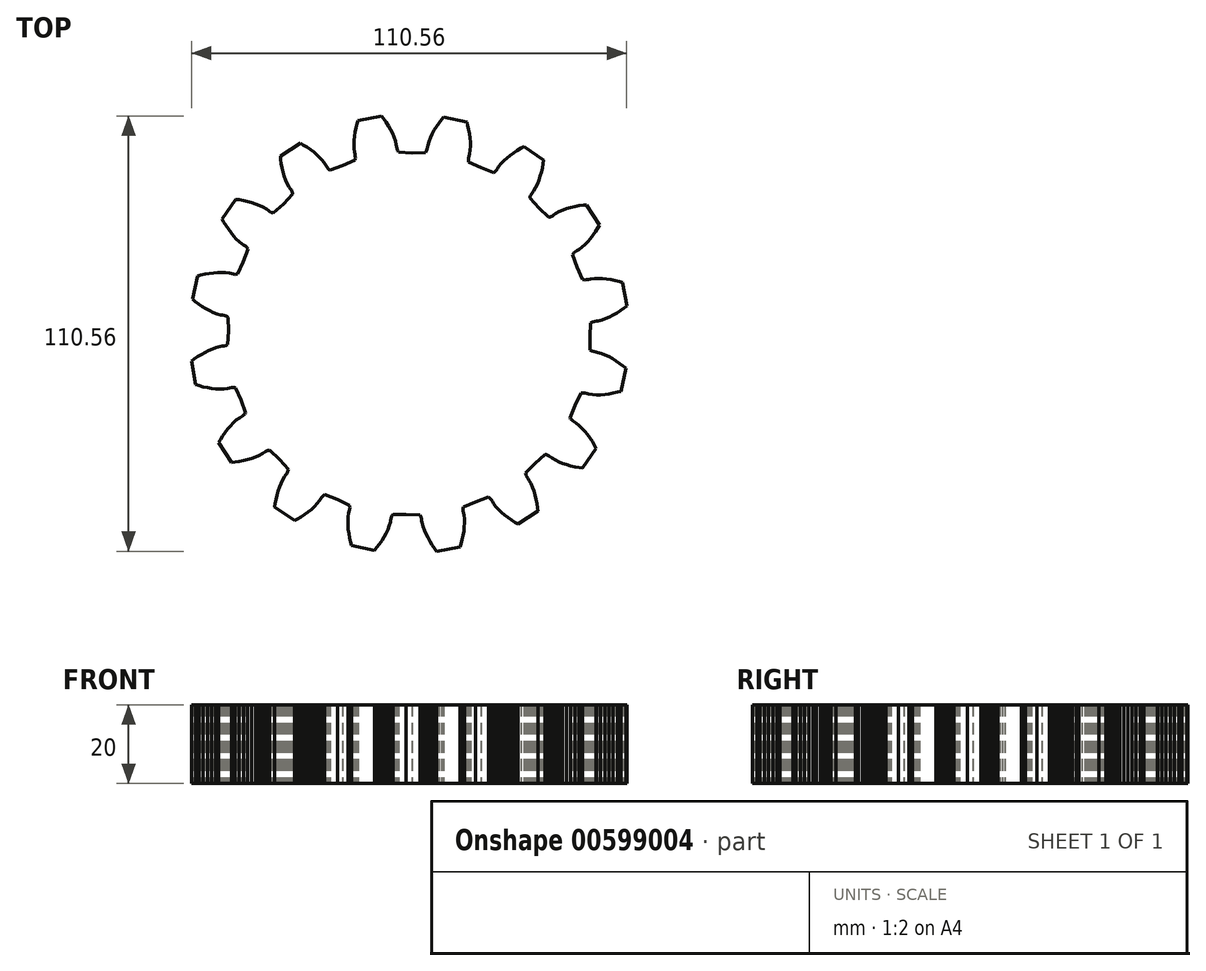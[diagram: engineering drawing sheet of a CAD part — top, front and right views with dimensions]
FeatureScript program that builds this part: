
annotation { "Feature Type Name" : "Feature", "Feature Type Description" : "" }
export const myFeature = defineFeature(function(context is Context, id is Id, definition is map)
    precondition{}
    {
        {
            var Q0;
            Q0=qCreatedBy(makeId("Top.planeOp"),FACE);
            var sketch = newSketch(context, id + "F0", { "sketchPlane" : qUnion([Q0])});
            skLineSegment(sketch, "E0", {"start": v(45.92, -0.72) * mm, "end": v(45.99, -4.15) * mm});
            skLineSegment(sketch, "E1", {"start": v(45.99, -4.15) * mm, "end": v(46.22, -4.32) * mm});
            skLineSegment(sketch, "E2", {"start": v(46.22, -4.32) * mm, "end": v(46.45, -4.43) * mm});
            skLineSegment(sketch, "E3", {"start": v(46.45, -4.43) * mm, "end": v(46.93, -4.6) * mm});
            skLineSegment(sketch, "E4", {"start": v(46.93, -4.6) * mm, "end": v(47.41, -4.7) * mm});
            skLineSegment(sketch, "E5", {"start": v(47.41, -4.7) * mm, "end": v(47.9, -4.78) * mm});
            skLineSegment(sketch, "E6", {"start": v(47.9, -4.78) * mm, "end": v(48.85, -5.05) * mm});
            skLineSegment(sketch, "E7", {"start": v(48.85, -5.05) * mm, "end": v(49.8, -5.41) * mm});
            skLineSegment(sketch, "E8", {"start": v(49.8, -5.41) * mm, "end": v(50.74, -5.86) * mm});
            skLineSegment(sketch, "E9", {"start": v(50.74, -5.86) * mm, "end": v(51.66, -6.36) * mm});
            skLineSegment(sketch, "E10", {"start": v(51.66, -6.36) * mm, "end": v(52.58, -6.93) * mm});
            skLineSegment(sketch, "E11", {"start": v(52.58, -6.93) * mm, "end": v(53.48, -7.54) * mm});
            skLineSegment(sketch, "E12", {"start": v(53.48, -7.54) * mm, "end": v(54.38, -8.21) * mm});
            skLineSegment(sketch, "E13", {"start": v(54.38, -8.21) * mm, "end": v(55.04, -8.75) * mm});
            skLineSegment(sketch, "E14", {"start": v(55.04, -8.75) * mm, "end": v(53.76, -14.67) * mm});
            skLineSegment(sketch, "E15", {"start": v(53.76, -14.67) * mm, "end": v(52.94, -14.89) * mm});
            skLineSegment(sketch, "E16", {"start": v(52.94, -14.89) * mm, "end": v(51.85, -15.13) * mm});
            skLineSegment(sketch, "E17", {"start": v(51.85, -15.13) * mm, "end": v(50.77, -15.32) * mm});
            skLineSegment(sketch, "E18", {"start": v(50.77, -15.32) * mm, "end": v(49.7, -15.46) * mm});
            skLineSegment(sketch, "E19", {"start": v(49.7, -15.46) * mm, "end": v(48.65, -15.54) * mm});
            skLineSegment(sketch, "E20", {"start": v(48.65, -15.54) * mm, "end": v(47.62, -15.56) * mm});
            skLineSegment(sketch, "E21", {"start": v(47.62, -15.56) * mm, "end": v(46.6, -15.5) * mm});
            skLineSegment(sketch, "E22", {"start": v(46.6, -15.5) * mm, "end": v(45.62, -15.36) * mm});
            skLineSegment(sketch, "E23", {"start": v(45.62, -15.36) * mm, "end": v(45.14, -15.23) * mm});
            skLineSegment(sketch, "E24", {"start": v(45.14, -15.23) * mm, "end": v(44.66, -15.12) * mm});
            skLineSegment(sketch, "E25", {"start": v(44.66, -15.12) * mm, "end": v(44.16, -15.07) * mm});
            skLineSegment(sketch, "E26", {"start": v(44.16, -15.07) * mm, "end": v(43.9, -15.08) * mm});
            skLineSegment(sketch, "E27", {"start": v(43.9, -15.08) * mm, "end": v(43.62, -15.14) * mm});
            skLineSegment(sketch, "E28", {"start": v(43.62, -15.14) * mm, "end": v(42.15, -18.24) * mm});
            skLineSegment(sketch, "E29", {"start": v(42.15, -18.24) * mm, "end": v(40.9, -21.43) * mm});
            skLineSegment(sketch, "E30", {"start": v(40.9, -21.43) * mm, "end": v(41.05, -21.68) * mm});
            skLineSegment(sketch, "E31", {"start": v(41.05, -21.68) * mm, "end": v(41.22, -21.87) * mm});
            skLineSegment(sketch, "E32", {"start": v(41.22, -21.87) * mm, "end": v(41.6, -22.2) * mm});
            skLineSegment(sketch, "E33", {"start": v(41.6, -22.2) * mm, "end": v(42, -22.48) * mm});
            skLineSegment(sketch, "E34", {"start": v(42, -22.48) * mm, "end": v(42.42, -22.74) * mm});
            skLineSegment(sketch, "E35", {"start": v(42.42, -22.74) * mm, "end": v(43.2, -23.36) * mm});
            skLineSegment(sketch, "E36", {"start": v(43.2, -23.36) * mm, "end": v(43.94, -24.06) * mm});
            skLineSegment(sketch, "E37", {"start": v(43.94, -24.06) * mm, "end": v(44.63, -24.83) * mm});
            skLineSegment(sketch, "E38", {"start": v(44.63, -24.83) * mm, "end": v(45.3, -25.65) * mm});
            skLineSegment(sketch, "E39", {"start": v(45.3, -25.65) * mm, "end": v(45.93, -26.52) * mm});
            skLineSegment(sketch, "E40", {"start": v(45.93, -26.52) * mm, "end": v(46.52, -27.44) * mm});
            skLineSegment(sketch, "E41", {"start": v(46.52, -27.44) * mm, "end": v(47.1, -28.4) * mm});
            skLineSegment(sketch, "E42", {"start": v(47.1, -28.4) * mm, "end": v(47.5, -29.14) * mm});
            skLineSegment(sketch, "E43", {"start": v(47.5, -29.14) * mm, "end": v(44.05, -34.13) * mm});
            skLineSegment(sketch, "E44", {"start": v(44.05, -34.13) * mm, "end": v(43.21, -34.01) * mm});
            skLineSegment(sketch, "E45", {"start": v(43.21, -34.01) * mm, "end": v(42.11, -33.82) * mm});
            skLineSegment(sketch, "E46", {"start": v(42.11, -33.82) * mm, "end": v(41.04, -33.59) * mm});
            skLineSegment(sketch, "E47", {"start": v(41.04, -33.59) * mm, "end": v(40, -33.3) * mm});
            skLineSegment(sketch, "E48", {"start": v(40, -33.3) * mm, "end": v(39, -32.98) * mm});
            skLineSegment(sketch, "E49", {"start": v(39, -32.98) * mm, "end": v(38.04, -32.6) * mm});
            skLineSegment(sketch, "E50", {"start": v(38.04, -32.6) * mm, "end": v(37.12, -32.16) * mm});
            skLineSegment(sketch, "E51", {"start": v(37.12, -32.16) * mm, "end": v(36.27, -31.65) * mm});
            skLineSegment(sketch, "E52", {"start": v(36.27, -31.65) * mm, "end": v(35.88, -31.35) * mm});
            skLineSegment(sketch, "E53", {"start": v(35.88, -31.35) * mm, "end": v(35.48, -31.06) * mm});
            skLineSegment(sketch, "E54", {"start": v(35.48, -31.06) * mm, "end": v(35.03, -30.83) * mm});
            skLineSegment(sketch, "E55", {"start": v(35.03, -30.83) * mm, "end": v(34.79, -30.74) * mm});
            skLineSegment(sketch, "E56", {"start": v(34.79, -30.74) * mm, "end": v(34.5, -30.68) * mm});
            skLineSegment(sketch, "E57", {"start": v(34.5, -30.68) * mm, "end": v(31.96, -32.98) * mm});
            skLineSegment(sketch, "E58", {"start": v(31.96, -32.98) * mm, "end": v(29.58, -35.45) * mm});
            skLineSegment(sketch, "E59", {"start": v(29.58, -35.45) * mm, "end": v(29.63, -35.73) * mm});
            skLineSegment(sketch, "E60", {"start": v(29.63, -35.73) * mm, "end": v(29.71, -35.98) * mm});
            skLineSegment(sketch, "E61", {"start": v(29.71, -35.98) * mm, "end": v(29.93, -36.43) * mm});
            skLineSegment(sketch, "E62", {"start": v(29.93, -36.43) * mm, "end": v(30.2, -36.85) * mm});
            skLineSegment(sketch, "E63", {"start": v(30.2, -36.85) * mm, "end": v(30.5, -37.25) * mm});
            skLineSegment(sketch, "E64", {"start": v(30.5, -37.25) * mm, "end": v(30.98, -38.11) * mm});
            skLineSegment(sketch, "E65", {"start": v(30.98, -38.11) * mm, "end": v(31.39, -39.04) * mm});
            skLineSegment(sketch, "E66", {"start": v(31.39, -39.04) * mm, "end": v(31.73, -40.02) * mm});
            skLineSegment(sketch, "E67", {"start": v(31.73, -40.02) * mm, "end": v(32.03, -41.03) * mm});
            skLineSegment(sketch, "E68", {"start": v(32.03, -41.03) * mm, "end": v(32.28, -42.08) * mm});
            skLineSegment(sketch, "E69", {"start": v(32.28, -42.08) * mm, "end": v(32.48, -43.15) * mm});
            skLineSegment(sketch, "E70", {"start": v(32.48, -43.15) * mm, "end": v(32.64, -44.26) * mm});
            skLineSegment(sketch, "E71", {"start": v(32.64, -44.26) * mm, "end": v(32.73, -45.1) * mm});
            skLineSegment(sketch, "E72", {"start": v(32.73, -45.1) * mm, "end": v(27.64, -48.4) * mm});
            skLineSegment(sketch, "E73", {"start": v(27.64, -48.4) * mm, "end": v(26.9, -47.96) * mm});
            skLineSegment(sketch, "E74", {"start": v(26.9, -47.96) * mm, "end": v(25.96, -47.36) * mm});
            skLineSegment(sketch, "E75", {"start": v(25.96, -47.36) * mm, "end": v(25.06, -46.74) * mm});
            skLineSegment(sketch, "E76", {"start": v(25.06, -46.74) * mm, "end": v(24.21, -46.08) * mm});
            skLineSegment(sketch, "E77", {"start": v(24.21, -46.08) * mm, "end": v(23.41, -45.4) * mm});
            skLineSegment(sketch, "E78", {"start": v(23.41, -45.4) * mm, "end": v(22.67, -44.67) * mm});
            skLineSegment(sketch, "E79", {"start": v(22.67, -44.67) * mm, "end": v(21.99, -43.92) * mm});
            skLineSegment(sketch, "E80", {"start": v(21.99, -43.92) * mm, "end": v(21.4, -43.12) * mm});
            skLineSegment(sketch, "E81", {"start": v(21.4, -43.12) * mm, "end": v(21.15, -42.7) * mm});
            skLineSegment(sketch, "E82", {"start": v(21.15, -42.7) * mm, "end": v(20.89, -42.28) * mm});
            skLineSegment(sketch, "E83", {"start": v(20.89, -42.28) * mm, "end": v(20.57, -41.89) * mm});
            skLineSegment(sketch, "E84", {"start": v(20.57, -41.89) * mm, "end": v(20.38, -41.7) * mm});
            skLineSegment(sketch, "E85", {"start": v(20.38, -41.7) * mm, "end": v(20.14, -41.55) * mm});
            skLineSegment(sketch, "E86", {"start": v(20.14, -41.55) * mm, "end": v(16.9, -42.7) * mm});
            skLineSegment(sketch, "E87", {"start": v(16.9, -42.7) * mm, "end": v(13.76, -44.08) * mm});
            skLineSegment(sketch, "E88", {"start": v(13.76, -44.08) * mm, "end": v(13.7, -44.35) * mm});
            skLineSegment(sketch, "E89", {"start": v(13.7, -44.35) * mm, "end": v(13.68, -44.61) * mm});
            skLineSegment(sketch, "E90", {"start": v(13.68, -44.61) * mm, "end": v(13.71, -45.12) * mm});
            skLineSegment(sketch, "E91", {"start": v(13.71, -45.12) * mm, "end": v(13.8, -45.6) * mm});
            skLineSegment(sketch, "E92", {"start": v(13.8, -45.6) * mm, "end": v(13.92, -46.08) * mm});
            skLineSegment(sketch, "E93", {"start": v(13.92, -46.08) * mm, "end": v(14.03, -47.07) * mm});
            skLineSegment(sketch, "E94", {"start": v(14.03, -47.07) * mm, "end": v(14.06, -48.08) * mm});
            skLineSegment(sketch, "E95", {"start": v(14.06, -48.08) * mm, "end": v(14, -49.12) * mm});
            skLineSegment(sketch, "E96", {"start": v(14, -49.12) * mm, "end": v(13.9, -50.17) * mm});
            skLineSegment(sketch, "E97", {"start": v(13.9, -50.17) * mm, "end": v(13.72, -51.23) * mm});
            skLineSegment(sketch, "E98", {"start": v(13.72, -51.23) * mm, "end": v(13.5, -52.3) * mm});
            skLineSegment(sketch, "E99", {"start": v(13.5, -52.3) * mm, "end": v(13.22, -53.38) * mm});
            skLineSegment(sketch, "E100", {"start": v(13.22, -53.38) * mm, "end": v(12.98, -54.2) * mm});
            skLineSegment(sketch, "E101", {"start": v(12.98, -54.2) * mm, "end": v(7.02, -55.28) * mm});
            skLineSegment(sketch, "E102", {"start": v(7.02, -55.28) * mm, "end": v(6.5, -54.6) * mm});
            skLineSegment(sketch, "E103", {"start": v(6.5, -54.6) * mm, "end": v(5.86, -53.7) * mm});
            skLineSegment(sketch, "E104", {"start": v(5.86, -53.7) * mm, "end": v(5.27, -52.77) * mm});
            skLineSegment(sketch, "E105", {"start": v(5.27, -52.77) * mm, "end": v(4.74, -51.84) * mm});
            skLineSegment(sketch, "E106", {"start": v(4.74, -51.84) * mm, "end": v(4.26, -50.9) * mm});
            skLineSegment(sketch, "E107", {"start": v(4.26, -50.9) * mm, "end": v(3.85, -49.95) * mm});
            skLineSegment(sketch, "E108", {"start": v(3.85, -49.95) * mm, "end": v(3.5, -48.99) * mm});
            skLineSegment(sketch, "E109", {"start": v(3.5, -48.99) * mm, "end": v(3.27, -48.02) * mm});
            skLineSegment(sketch, "E110", {"start": v(3.27, -48.02) * mm, "end": v(3.2, -47.54) * mm});
            skLineSegment(sketch, "E111", {"start": v(3.2, -47.54) * mm, "end": v(3.12, -47.05) * mm});
            skLineSegment(sketch, "E112", {"start": v(3.12, -47.05) * mm, "end": v(2.97, -46.57) * mm});
            skLineSegment(sketch, "E113", {"start": v(2.97, -46.57) * mm, "end": v(2.86, -46.33) * mm});
            skLineSegment(sketch, "E114", {"start": v(2.86, -46.33) * mm, "end": v(2.7, -46.1) * mm});
            skLineSegment(sketch, "E115", {"start": v(2.7, -46.1) * mm, "end": v(-0.72, -45.92) * mm});
            skLineSegment(sketch, "E116", {"start": v(-0.72, -45.92) * mm, "end": v(-4.15, -45.99) * mm});
            skLineSegment(sketch, "E117", {"start": v(-4.15, -45.99) * mm, "end": v(-4.32, -46.22) * mm});
            skLineSegment(sketch, "E118", {"start": v(-4.32, -46.22) * mm, "end": v(-4.43, -46.45) * mm});
            skLineSegment(sketch, "E119", {"start": v(-4.43, -46.45) * mm, "end": v(-4.6, -46.93) * mm});
            skLineSegment(sketch, "E120", {"start": v(-4.6, -46.93) * mm, "end": v(-4.7, -47.41) * mm});
            skLineSegment(sketch, "E121", {"start": v(-4.7, -47.41) * mm, "end": v(-4.78, -47.9) * mm});
            skLineSegment(sketch, "E122", {"start": v(-4.78, -47.9) * mm, "end": v(-5.05, -48.85) * mm});
            skLineSegment(sketch, "E123", {"start": v(-5.05, -48.85) * mm, "end": v(-5.41, -49.8) * mm});
            skLineSegment(sketch, "E124", {"start": v(-5.41, -49.8) * mm, "end": v(-5.86, -50.74) * mm});
            skLineSegment(sketch, "E125", {"start": v(-5.86, -50.74) * mm, "end": v(-6.36, -51.66) * mm});
            skLineSegment(sketch, "E126", {"start": v(-6.36, -51.66) * mm, "end": v(-6.93, -52.58) * mm});
            skLineSegment(sketch, "E127", {"start": v(-6.93, -52.58) * mm, "end": v(-7.54, -53.48) * mm});
            skLineSegment(sketch, "E128", {"start": v(-7.54, -53.48) * mm, "end": v(-8.21, -54.38) * mm});
            skLineSegment(sketch, "E129", {"start": v(-8.21, -54.38) * mm, "end": v(-8.75, -55.04) * mm});
            skLineSegment(sketch, "E130", {"start": v(-8.75, -55.04) * mm, "end": v(-14.67, -53.76) * mm});
            skLineSegment(sketch, "E131", {"start": v(-14.67, -53.76) * mm, "end": v(-14.89, -52.94) * mm});
            skLineSegment(sketch, "E132", {"start": v(-14.89, -52.94) * mm, "end": v(-15.13, -51.85) * mm});
            skLineSegment(sketch, "E133", {"start": v(-15.13, -51.85) * mm, "end": v(-15.32, -50.77) * mm});
            skLineSegment(sketch, "E134", {"start": v(-15.32, -50.77) * mm, "end": v(-15.46, -49.7) * mm});
            skLineSegment(sketch, "E135", {"start": v(-15.46, -49.7) * mm, "end": v(-15.54, -48.65) * mm});
            skLineSegment(sketch, "E136", {"start": v(-15.54, -48.65) * mm, "end": v(-15.56, -47.62) * mm});
            skLineSegment(sketch, "E137", {"start": v(-15.56, -47.62) * mm, "end": v(-15.5, -46.6) * mm});
            skLineSegment(sketch, "E138", {"start": v(-15.5, -46.6) * mm, "end": v(-15.36, -45.62) * mm});
            skLineSegment(sketch, "E139", {"start": v(-15.36, -45.62) * mm, "end": v(-15.23, -45.14) * mm});
            skLineSegment(sketch, "E140", {"start": v(-15.23, -45.14) * mm, "end": v(-15.12, -44.66) * mm});
            skLineSegment(sketch, "E141", {"start": v(-15.12, -44.66) * mm, "end": v(-15.07, -44.16) * mm});
            skLineSegment(sketch, "E142", {"start": v(-15.07, -44.16) * mm, "end": v(-15.08, -43.9) * mm});
            skLineSegment(sketch, "E143", {"start": v(-15.08, -43.9) * mm, "end": v(-15.14, -43.62) * mm});
            skLineSegment(sketch, "E144", {"start": v(-15.14, -43.62) * mm, "end": v(-18.24, -42.15) * mm});
            skLineSegment(sketch, "E145", {"start": v(-18.24, -42.15) * mm, "end": v(-21.43, -40.9) * mm});
            skLineSegment(sketch, "E146", {"start": v(-21.43, -40.9) * mm, "end": v(-21.68, -41.05) * mm});
            skLineSegment(sketch, "E147", {"start": v(-21.68, -41.05) * mm, "end": v(-21.87, -41.22) * mm});
            skLineSegment(sketch, "E148", {"start": v(-21.87, -41.22) * mm, "end": v(-22.2, -41.6) * mm});
            skLineSegment(sketch, "E149", {"start": v(-22.2, -41.6) * mm, "end": v(-22.48, -42) * mm});
            skLineSegment(sketch, "E150", {"start": v(-22.48, -42) * mm, "end": v(-22.74, -42.42) * mm});
            skLineSegment(sketch, "E151", {"start": v(-22.74, -42.42) * mm, "end": v(-23.36, -43.2) * mm});
            skLineSegment(sketch, "E152", {"start": v(-23.36, -43.2) * mm, "end": v(-24.06, -43.94) * mm});
            skLineSegment(sketch, "E153", {"start": v(-24.06, -43.94) * mm, "end": v(-24.83, -44.63) * mm});
            skLineSegment(sketch, "E154", {"start": v(-24.83, -44.63) * mm, "end": v(-25.65, -45.3) * mm});
            skLineSegment(sketch, "E155", {"start": v(-25.65, -45.3) * mm, "end": v(-26.52, -45.93) * mm});
            skLineSegment(sketch, "E156", {"start": v(-26.52, -45.93) * mm, "end": v(-27.44, -46.52) * mm});
            skLineSegment(sketch, "E157", {"start": v(-27.44, -46.52) * mm, "end": v(-28.4, -47.1) * mm});
            skLineSegment(sketch, "E158", {"start": v(-28.4, -47.1) * mm, "end": v(-29.14, -47.5) * mm});
            skLineSegment(sketch, "E159", {"start": v(-29.14, -47.5) * mm, "end": v(-34.13, -44.05) * mm});
            skLineSegment(sketch, "E160", {"start": v(-34.13, -44.05) * mm, "end": v(-34.01, -43.21) * mm});
            skLineSegment(sketch, "E161", {"start": v(-34.01, -43.21) * mm, "end": v(-33.82, -42.11) * mm});
            skLineSegment(sketch, "E162", {"start": v(-33.82, -42.11) * mm, "end": v(-33.59, -41.04) * mm});
            skLineSegment(sketch, "E163", {"start": v(-33.59, -41.04) * mm, "end": v(-33.3, -40) * mm});
            skLineSegment(sketch, "E164", {"start": v(-33.3, -40) * mm, "end": v(-32.98, -39) * mm});
            skLineSegment(sketch, "E165", {"start": v(-32.98, -39) * mm, "end": v(-32.6, -38.04) * mm});
            skLineSegment(sketch, "E166", {"start": v(-32.6, -38.04) * mm, "end": v(-32.16, -37.12) * mm});
            skLineSegment(sketch, "E167", {"start": v(-32.16, -37.12) * mm, "end": v(-31.65, -36.27) * mm});
            skLineSegment(sketch, "E168", {"start": v(-31.65, -36.27) * mm, "end": v(-31.35, -35.88) * mm});
            skLineSegment(sketch, "E169", {"start": v(-31.35, -35.88) * mm, "end": v(-31.06, -35.48) * mm});
            skLineSegment(sketch, "E170", {"start": v(-31.06, -35.48) * mm, "end": v(-30.83, -35.03) * mm});
            skLineSegment(sketch, "E171", {"start": v(-30.83, -35.03) * mm, "end": v(-30.74, -34.79) * mm});
            skLineSegment(sketch, "E172", {"start": v(-30.74, -34.79) * mm, "end": v(-30.68, -34.5) * mm});
            skLineSegment(sketch, "E173", {"start": v(-30.68, -34.5) * mm, "end": v(-32.98, -31.96) * mm});
            skLineSegment(sketch, "E174", {"start": v(-32.98, -31.96) * mm, "end": v(-35.45, -29.58) * mm});
            skLineSegment(sketch, "E175", {"start": v(-35.45, -29.58) * mm, "end": v(-35.73, -29.63) * mm});
            skLineSegment(sketch, "E176", {"start": v(-35.73, -29.63) * mm, "end": v(-35.98, -29.71) * mm});
            skLineSegment(sketch, "E177", {"start": v(-35.98, -29.71) * mm, "end": v(-36.43, -29.93) * mm});
            skLineSegment(sketch, "E178", {"start": v(-36.43, -29.93) * mm, "end": v(-36.85, -30.2) * mm});
            skLineSegment(sketch, "E179", {"start": v(-36.85, -30.2) * mm, "end": v(-37.25, -30.5) * mm});
            skLineSegment(sketch, "E180", {"start": v(-37.25, -30.5) * mm, "end": v(-38.11, -30.98) * mm});
            skLineSegment(sketch, "E181", {"start": v(-38.11, -30.98) * mm, "end": v(-39.04, -31.39) * mm});
            skLineSegment(sketch, "E182", {"start": v(-39.04, -31.39) * mm, "end": v(-40.02, -31.73) * mm});
            skLineSegment(sketch, "E183", {"start": v(-40.02, -31.73) * mm, "end": v(-41.03, -32.03) * mm});
            skLineSegment(sketch, "E184", {"start": v(-41.03, -32.03) * mm, "end": v(-42.08, -32.28) * mm});
            skLineSegment(sketch, "E185", {"start": v(-42.08, -32.28) * mm, "end": v(-43.15, -32.48) * mm});
            skLineSegment(sketch, "E186", {"start": v(-43.15, -32.48) * mm, "end": v(-44.26, -32.64) * mm});
            skLineSegment(sketch, "E187", {"start": v(-44.26, -32.64) * mm, "end": v(-45.1, -32.73) * mm});
            skLineSegment(sketch, "E188", {"start": v(-45.1, -32.73) * mm, "end": v(-48.4, -27.64) * mm});
            skLineSegment(sketch, "E189", {"start": v(-48.4, -27.64) * mm, "end": v(-47.96, -26.9) * mm});
            skLineSegment(sketch, "E190", {"start": v(-47.96, -26.9) * mm, "end": v(-47.36, -25.96) * mm});
            skLineSegment(sketch, "E191", {"start": v(-47.36, -25.96) * mm, "end": v(-46.74, -25.06) * mm});
            skLineSegment(sketch, "E192", {"start": v(-46.74, -25.06) * mm, "end": v(-46.08, -24.21) * mm});
            skLineSegment(sketch, "E193", {"start": v(-46.08, -24.21) * mm, "end": v(-45.4, -23.41) * mm});
            skLineSegment(sketch, "E194", {"start": v(-45.4, -23.41) * mm, "end": v(-44.67, -22.67) * mm});
            skLineSegment(sketch, "E195", {"start": v(-44.67, -22.67) * mm, "end": v(-43.92, -21.99) * mm});
            skLineSegment(sketch, "E196", {"start": v(-43.92, -21.99) * mm, "end": v(-43.12, -21.4) * mm});
            skLineSegment(sketch, "E197", {"start": v(-43.12, -21.4) * mm, "end": v(-42.7, -21.15) * mm});
            skLineSegment(sketch, "E198", {"start": v(-42.7, -21.15) * mm, "end": v(-42.28, -20.89) * mm});
            skLineSegment(sketch, "E199", {"start": v(-42.28, -20.89) * mm, "end": v(-41.89, -20.57) * mm});
            skLineSegment(sketch, "E200", {"start": v(-41.89, -20.57) * mm, "end": v(-41.7, -20.38) * mm});
            skLineSegment(sketch, "E201", {"start": v(-41.7, -20.38) * mm, "end": v(-41.55, -20.14) * mm});
            skLineSegment(sketch, "E202", {"start": v(-41.55, -20.14) * mm, "end": v(-42.7, -16.9) * mm});
            skLineSegment(sketch, "E203", {"start": v(-42.7, -16.9) * mm, "end": v(-44.08, -13.76) * mm});
            skLineSegment(sketch, "E204", {"start": v(-44.08, -13.76) * mm, "end": v(-44.35, -13.7) * mm});
            skLineSegment(sketch, "E205", {"start": v(-44.35, -13.7) * mm, "end": v(-44.61, -13.68) * mm});
            skLineSegment(sketch, "E206", {"start": v(-44.61, -13.68) * mm, "end": v(-45.12, -13.71) * mm});
            skLineSegment(sketch, "E207", {"start": v(-45.12, -13.71) * mm, "end": v(-45.6, -13.8) * mm});
            skLineSegment(sketch, "E208", {"start": v(-45.6, -13.8) * mm, "end": v(-46.08, -13.92) * mm});
            skLineSegment(sketch, "E209", {"start": v(-46.08, -13.92) * mm, "end": v(-47.07, -14.03) * mm});
            skLineSegment(sketch, "E210", {"start": v(-47.07, -14.03) * mm, "end": v(-48.08, -14.06) * mm});
            skLineSegment(sketch, "E211", {"start": v(-48.08, -14.06) * mm, "end": v(-49.12, -14) * mm});
            skLineSegment(sketch, "E212", {"start": v(-49.12, -14) * mm, "end": v(-50.17, -13.9) * mm});
            skLineSegment(sketch, "E213", {"start": v(-50.17, -13.9) * mm, "end": v(-51.23, -13.72) * mm});
            skLineSegment(sketch, "E214", {"start": v(-51.23, -13.72) * mm, "end": v(-52.3, -13.5) * mm});
            skLineSegment(sketch, "E215", {"start": v(-52.3, -13.5) * mm, "end": v(-53.38, -13.22) * mm});
            skLineSegment(sketch, "E216", {"start": v(-53.38, -13.22) * mm, "end": v(-54.2, -12.98) * mm});
            skLineSegment(sketch, "E217", {"start": v(-54.2, -12.98) * mm, "end": v(-55.28, -7.02) * mm});
            skLineSegment(sketch, "E218", {"start": v(-55.28, -7.02) * mm, "end": v(-54.6, -6.5) * mm});
            skLineSegment(sketch, "E219", {"start": v(-54.6, -6.5) * mm, "end": v(-53.7, -5.86) * mm});
            skLineSegment(sketch, "E220", {"start": v(-53.7, -5.86) * mm, "end": v(-52.77, -5.27) * mm});
            skLineSegment(sketch, "E221", {"start": v(-52.77, -5.27) * mm, "end": v(-51.84, -4.74) * mm});
            skLineSegment(sketch, "E222", {"start": v(-51.84, -4.74) * mm, "end": v(-50.9, -4.26) * mm});
            skLineSegment(sketch, "E223", {"start": v(-50.9, -4.26) * mm, "end": v(-49.95, -3.85) * mm});
            skLineSegment(sketch, "E224", {"start": v(-49.95, -3.85) * mm, "end": v(-48.99, -3.5) * mm});
            skLineSegment(sketch, "E225", {"start": v(-48.99, -3.5) * mm, "end": v(-48.02, -3.27) * mm});
            skLineSegment(sketch, "E226", {"start": v(-48.02, -3.27) * mm, "end": v(-47.54, -3.2) * mm});
            skLineSegment(sketch, "E227", {"start": v(-47.54, -3.2) * mm, "end": v(-47.05, -3.12) * mm});
            skLineSegment(sketch, "E228", {"start": v(-47.05, -3.12) * mm, "end": v(-46.57, -2.97) * mm});
            skLineSegment(sketch, "E229", {"start": v(-46.57, -2.97) * mm, "end": v(-46.33, -2.86) * mm});
            skLineSegment(sketch, "E230", {"start": v(-46.33, -2.86) * mm, "end": v(-46.1, -2.7) * mm});
            skLineSegment(sketch, "E231", {"start": v(-46.1, -2.7) * mm, "end": v(-45.92, 0.72) * mm});
            skLineSegment(sketch, "E232", {"start": v(-45.92, 0.72) * mm, "end": v(-45.99, 4.15) * mm});
            skLineSegment(sketch, "E233", {"start": v(-45.99, 4.15) * mm, "end": v(-46.22, 4.32) * mm});
            skLineSegment(sketch, "E234", {"start": v(-46.22, 4.32) * mm, "end": v(-46.45, 4.43) * mm});
            skLineSegment(sketch, "E235", {"start": v(-46.45, 4.43) * mm, "end": v(-46.93, 4.6) * mm});
            skLineSegment(sketch, "E236", {"start": v(-46.93, 4.6) * mm, "end": v(-47.41, 4.7) * mm});
            skLineSegment(sketch, "E237", {"start": v(-47.41, 4.7) * mm, "end": v(-47.9, 4.78) * mm});
            skLineSegment(sketch, "E238", {"start": v(-47.9, 4.78) * mm, "end": v(-48.85, 5.05) * mm});
            skLineSegment(sketch, "E239", {"start": v(-48.85, 5.05) * mm, "end": v(-49.8, 5.41) * mm});
            skLineSegment(sketch, "E240", {"start": v(-49.8, 5.41) * mm, "end": v(-50.74, 5.86) * mm});
            skLineSegment(sketch, "E241", {"start": v(-50.74, 5.86) * mm, "end": v(-51.66, 6.36) * mm});
            skLineSegment(sketch, "E242", {"start": v(-51.66, 6.36) * mm, "end": v(-52.58, 6.93) * mm});
            skLineSegment(sketch, "E243", {"start": v(-52.58, 6.93) * mm, "end": v(-53.48, 7.54) * mm});
            skLineSegment(sketch, "E244", {"start": v(-53.48, 7.54) * mm, "end": v(-54.38, 8.21) * mm});
            skLineSegment(sketch, "E245", {"start": v(-54.38, 8.21) * mm, "end": v(-55.04, 8.75) * mm});
            skLineSegment(sketch, "E246", {"start": v(-55.04, 8.75) * mm, "end": v(-53.76, 14.67) * mm});
            skLineSegment(sketch, "E247", {"start": v(-53.76, 14.67) * mm, "end": v(-52.94, 14.89) * mm});
            skLineSegment(sketch, "E248", {"start": v(-52.94, 14.89) * mm, "end": v(-51.85, 15.13) * mm});
            skLineSegment(sketch, "E249", {"start": v(-51.85, 15.13) * mm, "end": v(-50.77, 15.32) * mm});
            skLineSegment(sketch, "E250", {"start": v(-50.77, 15.32) * mm, "end": v(-49.7, 15.46) * mm});
            skLineSegment(sketch, "E251", {"start": v(-49.7, 15.46) * mm, "end": v(-48.65, 15.54) * mm});
            skLineSegment(sketch, "E252", {"start": v(-48.65, 15.54) * mm, "end": v(-47.62, 15.56) * mm});
            skLineSegment(sketch, "E253", {"start": v(-47.62, 15.56) * mm, "end": v(-46.6, 15.5) * mm});
            skLineSegment(sketch, "E254", {"start": v(-46.6, 15.5) * mm, "end": v(-45.62, 15.36) * mm});
            skLineSegment(sketch, "E255", {"start": v(-45.62, 15.36) * mm, "end": v(-45.14, 15.23) * mm});
            skLineSegment(sketch, "E256", {"start": v(-45.14, 15.23) * mm, "end": v(-44.66, 15.12) * mm});
            skLineSegment(sketch, "E257", {"start": v(-44.66, 15.12) * mm, "end": v(-44.16, 15.07) * mm});
            skLineSegment(sketch, "E258", {"start": v(-44.16, 15.07) * mm, "end": v(-43.9, 15.08) * mm});
            skLineSegment(sketch, "E259", {"start": v(-43.9, 15.08) * mm, "end": v(-43.62, 15.14) * mm});
            skLineSegment(sketch, "E260", {"start": v(-43.62, 15.14) * mm, "end": v(-42.15, 18.24) * mm});
            skLineSegment(sketch, "E261", {"start": v(-42.15, 18.24) * mm, "end": v(-40.9, 21.43) * mm});
            skLineSegment(sketch, "E262", {"start": v(-40.9, 21.43) * mm, "end": v(-41.05, 21.68) * mm});
            skLineSegment(sketch, "E263", {"start": v(-41.05, 21.68) * mm, "end": v(-41.22, 21.87) * mm});
            skLineSegment(sketch, "E264", {"start": v(-41.22, 21.87) * mm, "end": v(-41.6, 22.2) * mm});
            skLineSegment(sketch, "E265", {"start": v(-41.6, 22.2) * mm, "end": v(-42, 22.48) * mm});
            skLineSegment(sketch, "E266", {"start": v(-42, 22.48) * mm, "end": v(-42.42, 22.74) * mm});
            skLineSegment(sketch, "E267", {"start": v(-42.42, 22.74) * mm, "end": v(-43.2, 23.36) * mm});
            skLineSegment(sketch, "E268", {"start": v(-43.2, 23.36) * mm, "end": v(-43.94, 24.06) * mm});
            skLineSegment(sketch, "E269", {"start": v(-43.94, 24.06) * mm, "end": v(-44.63, 24.83) * mm});
            skLineSegment(sketch, "E270", {"start": v(-44.63, 24.83) * mm, "end": v(-45.3, 25.65) * mm});
            skLineSegment(sketch, "E271", {"start": v(-45.3, 25.65) * mm, "end": v(-45.93, 26.52) * mm});
            skLineSegment(sketch, "E272", {"start": v(-45.93, 26.52) * mm, "end": v(-46.52, 27.44) * mm});
            skLineSegment(sketch, "E273", {"start": v(-46.52, 27.44) * mm, "end": v(-47.1, 28.4) * mm});
            skLineSegment(sketch, "E274", {"start": v(-47.1, 28.4) * mm, "end": v(-47.5, 29.14) * mm});
            skLineSegment(sketch, "E275", {"start": v(-47.5, 29.14) * mm, "end": v(-44.05, 34.13) * mm});
            skLineSegment(sketch, "E276", {"start": v(-44.05, 34.13) * mm, "end": v(-43.21, 34.01) * mm});
            skLineSegment(sketch, "E277", {"start": v(-43.21, 34.01) * mm, "end": v(-42.11, 33.82) * mm});
            skLineSegment(sketch, "E278", {"start": v(-42.11, 33.82) * mm, "end": v(-41.04, 33.59) * mm});
            skLineSegment(sketch, "E279", {"start": v(-41.04, 33.59) * mm, "end": v(-40, 33.3) * mm});
            skLineSegment(sketch, "E280", {"start": v(-40, 33.3) * mm, "end": v(-39, 32.98) * mm});
            skLineSegment(sketch, "E281", {"start": v(-39, 32.98) * mm, "end": v(-38.04, 32.6) * mm});
            skLineSegment(sketch, "E282", {"start": v(-38.04, 32.6) * mm, "end": v(-37.12, 32.16) * mm});
            skLineSegment(sketch, "E283", {"start": v(-37.12, 32.16) * mm, "end": v(-36.27, 31.65) * mm});
            skLineSegment(sketch, "E284", {"start": v(-36.27, 31.65) * mm, "end": v(-35.88, 31.35) * mm});
            skLineSegment(sketch, "E285", {"start": v(-35.88, 31.35) * mm, "end": v(-35.48, 31.06) * mm});
            skLineSegment(sketch, "E286", {"start": v(-35.48, 31.06) * mm, "end": v(-35.03, 30.83) * mm});
            skLineSegment(sketch, "E287", {"start": v(-35.03, 30.83) * mm, "end": v(-34.79, 30.74) * mm});
            skLineSegment(sketch, "E288", {"start": v(-34.79, 30.74) * mm, "end": v(-34.5, 30.68) * mm});
            skLineSegment(sketch, "E289", {"start": v(-34.5, 30.68) * mm, "end": v(-31.96, 32.98) * mm});
            skLineSegment(sketch, "E290", {"start": v(-31.96, 32.98) * mm, "end": v(-29.58, 35.45) * mm});
            skLineSegment(sketch, "E291", {"start": v(-29.58, 35.45) * mm, "end": v(-29.63, 35.73) * mm});
            skLineSegment(sketch, "E292", {"start": v(-29.63, 35.73) * mm, "end": v(-29.71, 35.98) * mm});
            skLineSegment(sketch, "E293", {"start": v(-29.71, 35.98) * mm, "end": v(-29.93, 36.43) * mm});
            skLineSegment(sketch, "E294", {"start": v(-29.93, 36.43) * mm, "end": v(-30.2, 36.85) * mm});
            skLineSegment(sketch, "E295", {"start": v(-30.2, 36.85) * mm, "end": v(-30.5, 37.25) * mm});
            skLineSegment(sketch, "E296", {"start": v(-30.5, 37.25) * mm, "end": v(-30.98, 38.11) * mm});
            skLineSegment(sketch, "E297", {"start": v(-30.98, 38.11) * mm, "end": v(-31.39, 39.04) * mm});
            skLineSegment(sketch, "E298", {"start": v(-31.39, 39.04) * mm, "end": v(-31.73, 40.02) * mm});
            skLineSegment(sketch, "E299", {"start": v(-31.73, 40.02) * mm, "end": v(-32.03, 41.03) * mm});
            skLineSegment(sketch, "E300", {"start": v(-32.03, 41.03) * mm, "end": v(-32.28, 42.08) * mm});
            skLineSegment(sketch, "E301", {"start": v(-32.28, 42.08) * mm, "end": v(-32.48, 43.15) * mm});
            skLineSegment(sketch, "E302", {"start": v(-32.48, 43.15) * mm, "end": v(-32.64, 44.26) * mm});
            skLineSegment(sketch, "E303", {"start": v(-32.64, 44.26) * mm, "end": v(-32.73, 45.1) * mm});
            skLineSegment(sketch, "E304", {"start": v(-32.73, 45.1) * mm, "end": v(-27.64, 48.4) * mm});
            skLineSegment(sketch, "E305", {"start": v(-27.64, 48.4) * mm, "end": v(-26.9, 47.96) * mm});
            skLineSegment(sketch, "E306", {"start": v(-26.9, 47.96) * mm, "end": v(-25.96, 47.36) * mm});
            skLineSegment(sketch, "E307", {"start": v(-25.96, 47.36) * mm, "end": v(-25.06, 46.74) * mm});
            skLineSegment(sketch, "E308", {"start": v(-25.06, 46.74) * mm, "end": v(-24.21, 46.08) * mm});
            skLineSegment(sketch, "E309", {"start": v(-24.21, 46.08) * mm, "end": v(-23.41, 45.4) * mm});
            skLineSegment(sketch, "E310", {"start": v(-23.41, 45.4) * mm, "end": v(-22.67, 44.67) * mm});
            skLineSegment(sketch, "E311", {"start": v(-22.67, 44.67) * mm, "end": v(-21.99, 43.92) * mm});
            skLineSegment(sketch, "E312", {"start": v(-21.99, 43.92) * mm, "end": v(-21.4, 43.12) * mm});
            skLineSegment(sketch, "E313", {"start": v(-21.4, 43.12) * mm, "end": v(-21.15, 42.7) * mm});
            skLineSegment(sketch, "E314", {"start": v(-21.15, 42.7) * mm, "end": v(-20.89, 42.28) * mm});
            skLineSegment(sketch, "E315", {"start": v(-20.89, 42.28) * mm, "end": v(-20.57, 41.89) * mm});
            skLineSegment(sketch, "E316", {"start": v(-20.57, 41.89) * mm, "end": v(-20.38, 41.7) * mm});
            skLineSegment(sketch, "E317", {"start": v(-20.38, 41.7) * mm, "end": v(-20.14, 41.55) * mm});
            skLineSegment(sketch, "E318", {"start": v(-20.14, 41.55) * mm, "end": v(-16.9, 42.7) * mm});
            skLineSegment(sketch, "E319", {"start": v(-16.9, 42.7) * mm, "end": v(-13.76, 44.08) * mm});
            skLineSegment(sketch, "E320", {"start": v(-13.76, 44.08) * mm, "end": v(-13.7, 44.35) * mm});
            skLineSegment(sketch, "E321", {"start": v(-13.7, 44.35) * mm, "end": v(-13.68, 44.61) * mm});
            skLineSegment(sketch, "E322", {"start": v(-13.68, 44.61) * mm, "end": v(-13.71, 45.12) * mm});
            skLineSegment(sketch, "E323", {"start": v(-13.71, 45.12) * mm, "end": v(-13.8, 45.6) * mm});
            skLineSegment(sketch, "E324", {"start": v(-13.8, 45.6) * mm, "end": v(-13.92, 46.08) * mm});
            skLineSegment(sketch, "E325", {"start": v(-13.92, 46.08) * mm, "end": v(-14.03, 47.07) * mm});
            skLineSegment(sketch, "E326", {"start": v(-14.03, 47.07) * mm, "end": v(-14.06, 48.08) * mm});
            skLineSegment(sketch, "E327", {"start": v(-14.06, 48.08) * mm, "end": v(-14, 49.12) * mm});
            skLineSegment(sketch, "E328", {"start": v(-14, 49.12) * mm, "end": v(-13.9, 50.17) * mm});
            skLineSegment(sketch, "E329", {"start": v(-13.9, 50.17) * mm, "end": v(-13.72, 51.23) * mm});
            skLineSegment(sketch, "E330", {"start": v(-13.72, 51.23) * mm, "end": v(-13.5, 52.3) * mm});
            skLineSegment(sketch, "E331", {"start": v(-13.5, 52.3) * mm, "end": v(-13.22, 53.38) * mm});
            skLineSegment(sketch, "E332", {"start": v(-13.22, 53.38) * mm, "end": v(-12.98, 54.2) * mm});
            skLineSegment(sketch, "E333", {"start": v(-12.98, 54.2) * mm, "end": v(-7.02, 55.28) * mm});
            skLineSegment(sketch, "E334", {"start": v(-7.02, 55.28) * mm, "end": v(-6.5, 54.6) * mm});
            skLineSegment(sketch, "E335", {"start": v(-6.5, 54.6) * mm, "end": v(-5.86, 53.7) * mm});
            skLineSegment(sketch, "E336", {"start": v(-5.86, 53.7) * mm, "end": v(-5.27, 52.77) * mm});
            skLineSegment(sketch, "E337", {"start": v(-5.27, 52.77) * mm, "end": v(-4.74, 51.84) * mm});
            skLineSegment(sketch, "E338", {"start": v(-4.74, 51.84) * mm, "end": v(-4.26, 50.9) * mm});
            skLineSegment(sketch, "E339", {"start": v(-4.26, 50.9) * mm, "end": v(-3.85, 49.95) * mm});
            skLineSegment(sketch, "E340", {"start": v(-3.85, 49.95) * mm, "end": v(-3.5, 48.99) * mm});
            skLineSegment(sketch, "E341", {"start": v(-3.5, 48.99) * mm, "end": v(-3.27, 48.02) * mm});
            skLineSegment(sketch, "E342", {"start": v(-3.27, 48.02) * mm, "end": v(-3.2, 47.54) * mm});
            skLineSegment(sketch, "E343", {"start": v(-3.2, 47.54) * mm, "end": v(-3.12, 47.05) * mm});
            skLineSegment(sketch, "E344", {"start": v(-3.12, 47.05) * mm, "end": v(-2.97, 46.57) * mm});
            skLineSegment(sketch, "E345", {"start": v(-2.97, 46.57) * mm, "end": v(-2.86, 46.33) * mm});
            skLineSegment(sketch, "E346", {"start": v(-2.86, 46.33) * mm, "end": v(-2.7, 46.1) * mm});
            skLineSegment(sketch, "E347", {"start": v(-2.7, 46.1) * mm, "end": v(0.72, 45.92) * mm});
            skLineSegment(sketch, "E348", {"start": v(0.72, 45.92) * mm, "end": v(4.15, 45.99) * mm});
            skLineSegment(sketch, "E349", {"start": v(4.15, 45.99) * mm, "end": v(4.32, 46.22) * mm});
            skLineSegment(sketch, "E350", {"start": v(4.32, 46.22) * mm, "end": v(4.43, 46.45) * mm});
            skLineSegment(sketch, "E351", {"start": v(4.43, 46.45) * mm, "end": v(4.6, 46.93) * mm});
            skLineSegment(sketch, "E352", {"start": v(4.6, 46.93) * mm, "end": v(4.7, 47.41) * mm});
            skLineSegment(sketch, "E353", {"start": v(4.7, 47.41) * mm, "end": v(4.78, 47.9) * mm});
            skLineSegment(sketch, "E354", {"start": v(4.78, 47.9) * mm, "end": v(5.05, 48.85) * mm});
            skLineSegment(sketch, "E355", {"start": v(5.05, 48.85) * mm, "end": v(5.41, 49.8) * mm});
            skLineSegment(sketch, "E356", {"start": v(5.41, 49.8) * mm, "end": v(5.86, 50.74) * mm});
            skLineSegment(sketch, "E357", {"start": v(5.86, 50.74) * mm, "end": v(6.36, 51.66) * mm});
            skLineSegment(sketch, "E358", {"start": v(6.36, 51.66) * mm, "end": v(6.93, 52.58) * mm});
            skLineSegment(sketch, "E359", {"start": v(6.93, 52.58) * mm, "end": v(7.54, 53.48) * mm});
            skLineSegment(sketch, "E360", {"start": v(7.54, 53.48) * mm, "end": v(8.21, 54.38) * mm});
            skLineSegment(sketch, "E361", {"start": v(8.21, 54.38) * mm, "end": v(8.75, 55.04) * mm});
            skLineSegment(sketch, "E362", {"start": v(8.75, 55.04) * mm, "end": v(14.67, 53.76) * mm});
            skLineSegment(sketch, "E363", {"start": v(14.67, 53.76) * mm, "end": v(14.89, 52.94) * mm});
            skLineSegment(sketch, "E364", {"start": v(14.89, 52.94) * mm, "end": v(15.13, 51.85) * mm});
            skLineSegment(sketch, "E365", {"start": v(15.13, 51.85) * mm, "end": v(15.32, 50.77) * mm});
            skLineSegment(sketch, "E366", {"start": v(15.32, 50.77) * mm, "end": v(15.46, 49.7) * mm});
            skLineSegment(sketch, "E367", {"start": v(15.46, 49.7) * mm, "end": v(15.54, 48.65) * mm});
            skLineSegment(sketch, "E368", {"start": v(15.54, 48.65) * mm, "end": v(15.56, 47.62) * mm});
            skLineSegment(sketch, "E369", {"start": v(15.56, 47.62) * mm, "end": v(15.5, 46.6) * mm});
            skLineSegment(sketch, "E370", {"start": v(15.5, 46.6) * mm, "end": v(15.36, 45.62) * mm});
            skLineSegment(sketch, "E371", {"start": v(15.36, 45.62) * mm, "end": v(15.23, 45.14) * mm});
            skLineSegment(sketch, "E372", {"start": v(15.23, 45.14) * mm, "end": v(15.12, 44.66) * mm});
            skLineSegment(sketch, "E373", {"start": v(15.12, 44.66) * mm, "end": v(15.07, 44.16) * mm});
            skLineSegment(sketch, "E374", {"start": v(15.07, 44.16) * mm, "end": v(15.08, 43.9) * mm});
            skLineSegment(sketch, "E375", {"start": v(15.08, 43.9) * mm, "end": v(15.14, 43.62) * mm});
            skLineSegment(sketch, "E376", {"start": v(15.14, 43.62) * mm, "end": v(18.24, 42.15) * mm});
            skLineSegment(sketch, "E377", {"start": v(18.24, 42.15) * mm, "end": v(21.43, 40.9) * mm});
            skLineSegment(sketch, "E378", {"start": v(21.43, 40.9) * mm, "end": v(21.68, 41.05) * mm});
            skLineSegment(sketch, "E379", {"start": v(21.68, 41.05) * mm, "end": v(21.87, 41.22) * mm});
            skLineSegment(sketch, "E380", {"start": v(21.87, 41.22) * mm, "end": v(22.2, 41.6) * mm});
            skLineSegment(sketch, "E381", {"start": v(22.2, 41.6) * mm, "end": v(22.48, 42) * mm});
            skLineSegment(sketch, "E382", {"start": v(22.48, 42) * mm, "end": v(22.74, 42.42) * mm});
            skLineSegment(sketch, "E383", {"start": v(22.74, 42.42) * mm, "end": v(23.36, 43.2) * mm});
            skLineSegment(sketch, "E384", {"start": v(23.36, 43.2) * mm, "end": v(24.06, 43.94) * mm});
            skLineSegment(sketch, "E385", {"start": v(24.06, 43.94) * mm, "end": v(24.83, 44.63) * mm});
            skLineSegment(sketch, "E386", {"start": v(24.83, 44.63) * mm, "end": v(25.65, 45.3) * mm});
            skLineSegment(sketch, "E387", {"start": v(25.65, 45.3) * mm, "end": v(26.52, 45.93) * mm});
            skLineSegment(sketch, "E388", {"start": v(26.52, 45.93) * mm, "end": v(27.44, 46.52) * mm});
            skLineSegment(sketch, "E389", {"start": v(27.44, 46.52) * mm, "end": v(28.4, 47.1) * mm});
            skLineSegment(sketch, "E390", {"start": v(28.4, 47.1) * mm, "end": v(29.14, 47.5) * mm});
            skLineSegment(sketch, "E391", {"start": v(29.14, 47.5) * mm, "end": v(34.13, 44.05) * mm});
            skLineSegment(sketch, "E392", {"start": v(34.13, 44.05) * mm, "end": v(34.01, 43.21) * mm});
            skLineSegment(sketch, "E393", {"start": v(34.01, 43.21) * mm, "end": v(33.82, 42.11) * mm});
            skLineSegment(sketch, "E394", {"start": v(33.82, 42.11) * mm, "end": v(33.59, 41.04) * mm});
            skLineSegment(sketch, "E395", {"start": v(33.59, 41.04) * mm, "end": v(33.3, 40) * mm});
            skLineSegment(sketch, "E396", {"start": v(33.3, 40) * mm, "end": v(32.98, 39) * mm});
            skLineSegment(sketch, "E397", {"start": v(32.98, 39) * mm, "end": v(32.6, 38.04) * mm});
            skLineSegment(sketch, "E398", {"start": v(32.6, 38.04) * mm, "end": v(32.16, 37.12) * mm});
            skLineSegment(sketch, "E399", {"start": v(32.16, 37.12) * mm, "end": v(31.65, 36.27) * mm});
            skLineSegment(sketch, "E400", {"start": v(31.65, 36.27) * mm, "end": v(31.35, 35.88) * mm});
            skLineSegment(sketch, "E401", {"start": v(31.35, 35.88) * mm, "end": v(31.06, 35.48) * mm});
            skLineSegment(sketch, "E402", {"start": v(31.06, 35.48) * mm, "end": v(30.83, 35.03) * mm});
            skLineSegment(sketch, "E403", {"start": v(30.83, 35.03) * mm, "end": v(30.74, 34.79) * mm});
            skLineSegment(sketch, "E404", {"start": v(30.74, 34.79) * mm, "end": v(30.68, 34.5) * mm});
            skLineSegment(sketch, "E405", {"start": v(30.68, 34.5) * mm, "end": v(32.98, 31.96) * mm});
            skLineSegment(sketch, "E406", {"start": v(32.98, 31.96) * mm, "end": v(35.45, 29.58) * mm});
            skLineSegment(sketch, "E407", {"start": v(35.45, 29.58) * mm, "end": v(35.73, 29.63) * mm});
            skLineSegment(sketch, "E408", {"start": v(35.73, 29.63) * mm, "end": v(35.98, 29.71) * mm});
            skLineSegment(sketch, "E409", {"start": v(35.98, 29.71) * mm, "end": v(36.43, 29.93) * mm});
            skLineSegment(sketch, "E410", {"start": v(36.43, 29.93) * mm, "end": v(36.85, 30.2) * mm});
            skLineSegment(sketch, "E411", {"start": v(36.85, 30.2) * mm, "end": v(37.25, 30.5) * mm});
            skLineSegment(sketch, "E412", {"start": v(37.25, 30.5) * mm, "end": v(38.11, 30.98) * mm});
            skLineSegment(sketch, "E413", {"start": v(38.11, 30.98) * mm, "end": v(39.04, 31.39) * mm});
            skLineSegment(sketch, "E414", {"start": v(39.04, 31.39) * mm, "end": v(40.02, 31.73) * mm});
            skLineSegment(sketch, "E415", {"start": v(40.02, 31.73) * mm, "end": v(41.03, 32.03) * mm});
            skLineSegment(sketch, "E416", {"start": v(41.03, 32.03) * mm, "end": v(42.08, 32.28) * mm});
            skLineSegment(sketch, "E417", {"start": v(42.08, 32.28) * mm, "end": v(43.15, 32.48) * mm});
            skLineSegment(sketch, "E418", {"start": v(43.15, 32.48) * mm, "end": v(44.26, 32.64) * mm});
            skLineSegment(sketch, "E419", {"start": v(44.26, 32.64) * mm, "end": v(45.1, 32.73) * mm});
            skLineSegment(sketch, "E420", {"start": v(45.1, 32.73) * mm, "end": v(48.4, 27.64) * mm});
            skLineSegment(sketch, "E421", {"start": v(48.4, 27.64) * mm, "end": v(47.96, 26.9) * mm});
            skLineSegment(sketch, "E422", {"start": v(47.96, 26.9) * mm, "end": v(47.36, 25.96) * mm});
            skLineSegment(sketch, "E423", {"start": v(47.36, 25.96) * mm, "end": v(46.74, 25.06) * mm});
            skLineSegment(sketch, "E424", {"start": v(46.74, 25.06) * mm, "end": v(46.08, 24.21) * mm});
            skLineSegment(sketch, "E425", {"start": v(46.08, 24.21) * mm, "end": v(45.4, 23.41) * mm});
            skLineSegment(sketch, "E426", {"start": v(45.4, 23.41) * mm, "end": v(44.67, 22.67) * mm});
            skLineSegment(sketch, "E427", {"start": v(44.67, 22.67) * mm, "end": v(43.92, 21.99) * mm});
            skLineSegment(sketch, "E428", {"start": v(43.92, 21.99) * mm, "end": v(43.12, 21.4) * mm});
            skLineSegment(sketch, "E429", {"start": v(43.12, 21.4) * mm, "end": v(42.7, 21.15) * mm});
            skLineSegment(sketch, "E430", {"start": v(42.7, 21.15) * mm, "end": v(42.28, 20.89) * mm});
            skLineSegment(sketch, "E431", {"start": v(42.28, 20.89) * mm, "end": v(41.89, 20.57) * mm});
            skLineSegment(sketch, "E432", {"start": v(41.89, 20.57) * mm, "end": v(41.7, 20.38) * mm});
            skLineSegment(sketch, "E433", {"start": v(41.7, 20.38) * mm, "end": v(41.55, 20.14) * mm});
            skLineSegment(sketch, "E434", {"start": v(41.55, 20.14) * mm, "end": v(42.7, 16.9) * mm});
            skLineSegment(sketch, "E435", {"start": v(42.7, 16.9) * mm, "end": v(44.08, 13.76) * mm});
            skLineSegment(sketch, "E436", {"start": v(44.08, 13.76) * mm, "end": v(44.35, 13.7) * mm});
            skLineSegment(sketch, "E437", {"start": v(44.35, 13.7) * mm, "end": v(44.61, 13.68) * mm});
            skLineSegment(sketch, "E438", {"start": v(44.61, 13.68) * mm, "end": v(45.12, 13.71) * mm});
            skLineSegment(sketch, "E439", {"start": v(45.12, 13.71) * mm, "end": v(45.6, 13.8) * mm});
            skLineSegment(sketch, "E440", {"start": v(45.6, 13.8) * mm, "end": v(46.08, 13.92) * mm});
            skLineSegment(sketch, "E441", {"start": v(46.08, 13.92) * mm, "end": v(47.07, 14.03) * mm});
            skLineSegment(sketch, "E442", {"start": v(47.07, 14.03) * mm, "end": v(48.08, 14.06) * mm});
            skLineSegment(sketch, "E443", {"start": v(48.08, 14.06) * mm, "end": v(49.12, 14) * mm});
            skLineSegment(sketch, "E444", {"start": v(49.12, 14) * mm, "end": v(50.17, 13.9) * mm});
            skLineSegment(sketch, "E445", {"start": v(50.17, 13.9) * mm, "end": v(51.23, 13.72) * mm});
            skLineSegment(sketch, "E446", {"start": v(51.23, 13.72) * mm, "end": v(52.3, 13.5) * mm});
            skLineSegment(sketch, "E447", {"start": v(52.3, 13.5) * mm, "end": v(53.38, 13.22) * mm});
            skLineSegment(sketch, "E448", {"start": v(53.38, 13.22) * mm, "end": v(54.2, 12.98) * mm});
            skLineSegment(sketch, "E449", {"start": v(54.2, 12.98) * mm, "end": v(55.28, 7.02) * mm});
            skLineSegment(sketch, "E450", {"start": v(55.28, 7.02) * mm, "end": v(54.6, 6.5) * mm});
            skLineSegment(sketch, "E451", {"start": v(54.6, 6.5) * mm, "end": v(53.7, 5.86) * mm});
            skLineSegment(sketch, "E452", {"start": v(53.7, 5.86) * mm, "end": v(52.77, 5.27) * mm});
            skLineSegment(sketch, "E453", {"start": v(52.77, 5.27) * mm, "end": v(51.84, 4.74) * mm});
            skLineSegment(sketch, "E454", {"start": v(51.84, 4.74) * mm, "end": v(50.9, 4.26) * mm});
            skLineSegment(sketch, "E455", {"start": v(50.9, 4.26) * mm, "end": v(49.95, 3.85) * mm});
            skLineSegment(sketch, "E456", {"start": v(49.95, 3.85) * mm, "end": v(48.99, 3.5) * mm});
            skLineSegment(sketch, "E457", {"start": v(48.99, 3.5) * mm, "end": v(48.02, 3.27) * mm});
            skLineSegment(sketch, "E458", {"start": v(48.02, 3.27) * mm, "end": v(47.54, 3.2) * mm});
            skLineSegment(sketch, "E459", {"start": v(47.54, 3.2) * mm, "end": v(47.05, 3.12) * mm});
            skLineSegment(sketch, "E460", {"start": v(47.05, 3.12) * mm, "end": v(46.57, 2.97) * mm});
            skLineSegment(sketch, "E461", {"start": v(46.57, 2.97) * mm, "end": v(46.33, 2.86) * mm});
            skLineSegment(sketch, "E462", {"start": v(46.33, 2.86) * mm, "end": v(46.1, 2.7) * mm});
            skLineSegment(sketch, "E463", {"start": v(46.1, 2.7) * mm, "end": v(45.92, -0.72) * mm});
            skSolve(sketch);
        }
        {
            var Q0;
            Q0=makeQuery(id+"F0.imprint","IMPRINT",FACE,{"disambiguationData":[TD([[makeQuery(id+"F0.imprint","IMPRINT",EDGE,{"derivedFrom":sQuery(id+"F0.wireOp",EDGE,"E0")}),-1.0]])]});
            extrude(context, id + "F1", {"entities" : qUnion([Q0]), "depth" : 20 * mm, "offsetDistance" : 25 * mm});
        }
    });
